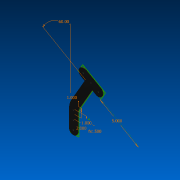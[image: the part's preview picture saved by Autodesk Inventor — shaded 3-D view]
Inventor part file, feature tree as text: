
AUTODESK INVENTOR PART (.ipt)
format: ipt  version: 2022.2 (Build 262287000, 287)  size: 128,512 bytes
history: native  units: in
note: dims shown in document units (in); Inventor stores cm internally (conversion verified against a paired STEP export)
features: sketch x1, extrude x1, hole x1, fillet x1
ambient origin geometry x8: Origin, YZ Plane, XZ Plane, XY Plane, X Axis, Y Axis, Z Axis, Center Point
bodies: Solid1 (feature_tree)
feature tree (4):
  sketch  "Sketch1"  dims[d0=1.0in d1=2.0in d2=1.0in d3=0.5in d4=0.125in d5=0.0in d6=60.0deg d7=0.175in d8=0.75in d9=0.375in d10=0.25in d11=0.5635in d12=1.0in d13=0.8108in d14=5.0in d15=0.5in]
  extrude  "Extrusion1"  Depth=0.5in
  hole  "Hole1"  [1 undecoded]
  fillet  "Fillet1"  Radius=0.5in
note: 1 required parameter value undecoded (feature->parameter linkage not recoverable at this tier; creation-order binding heuristic only, values carry confidence <= 0.55)
